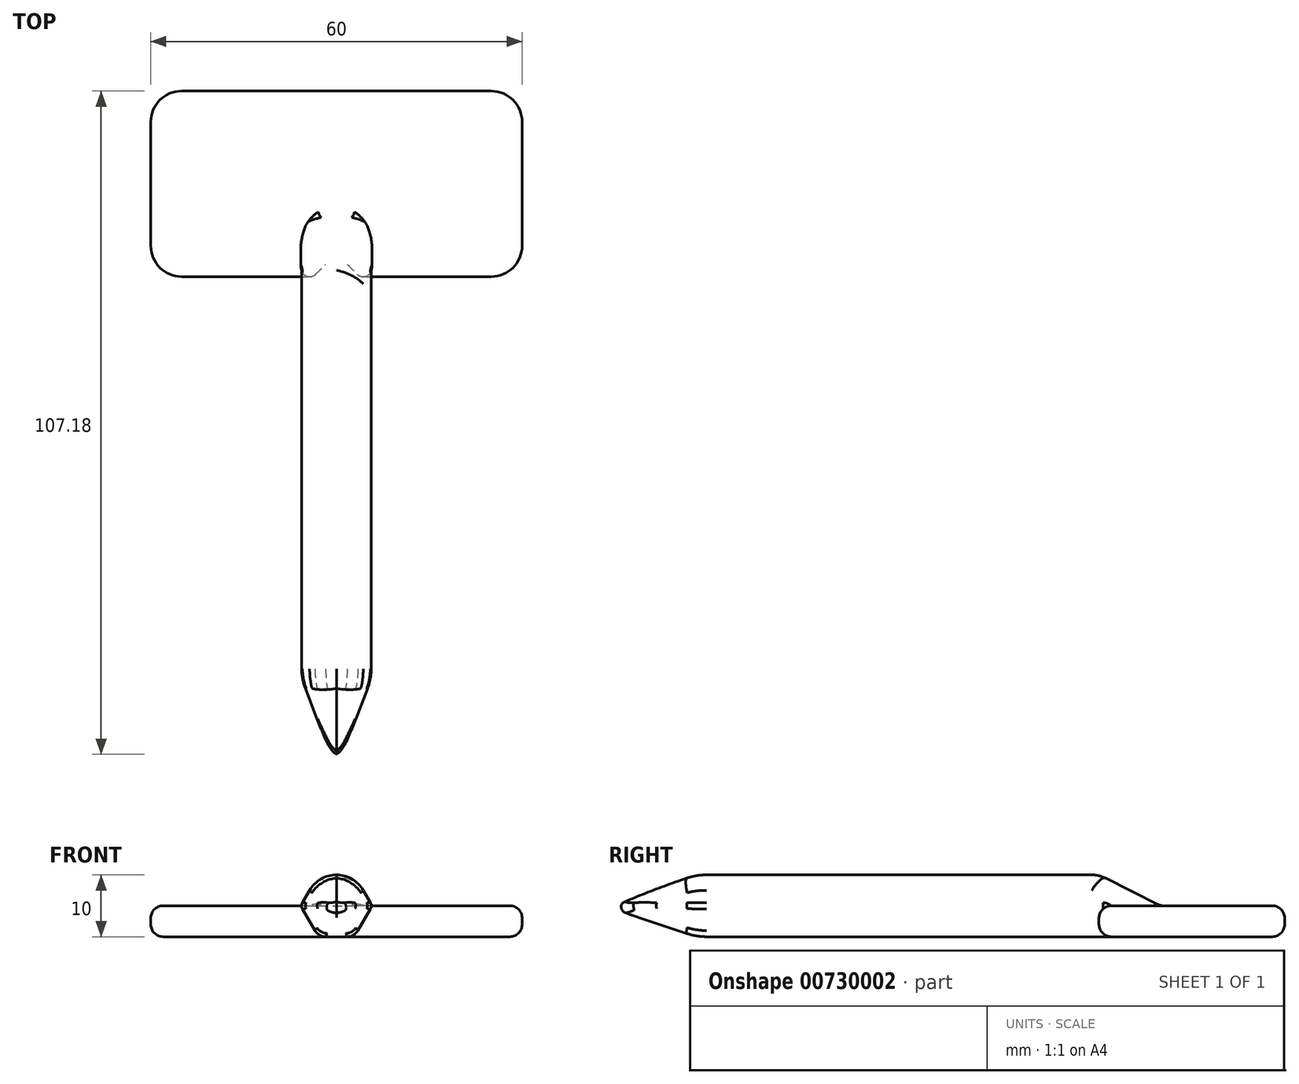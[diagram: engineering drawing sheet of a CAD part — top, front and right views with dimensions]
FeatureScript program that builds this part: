
annotation { "Feature Type Name" : "Feature", "Feature Type Description" : "" }
export const myFeature = defineFeature(function(context is Context, id is Id, definition is map)
    precondition{}
    {
        {
            var Q0;
            Q0=qCreatedBy(makeId("Top.planeOp"),FACE);
            var sketch = newSketch(context, id + "F0", { "sketchPlane" : qUnion([Q0])});
            skLineSegment(sketch, "E0.bottom", {"start": v(-30, 15) * mm, "end": v(30, 15) * mm});
            skLineSegment(sketch, "E0.top", {"start": v(-30, -15) * mm, "end": v(30, -15) * mm});
            skLineSegment(sketch, "E0.left", {"start": v(-30, 15) * mm, "end": v(-30, -15) * mm});
            skLineSegment(sketch, "E0.right", {"start": v(30, 15) * mm, "end": v(30, -15) * mm});
            skPoint(sketch, "E0.middle", {"position": v(0, 0) * mm});
            skSolve(sketch);
        }
        {
            var Q0;
            Q0=makeQuery(id+"F0.imprint","IMPRINT",FACE,{"disambiguationData":[TD([[makeQuery(id+"F0.imprint","IMPRINT",EDGE,{"derivedFrom":sQuery(id+"F0.wireOp",EDGE,"E0.bottom")}),-1.0]])]});
            extrude(context, id + "F1", {"entities" : qUnion([Q0]), "depth" : 5 * mm, "offsetDistance" : 25 * mm});
        }
        {
            var Q0;
            Q0=makeQuery(id+"F1.opExtrude","SWEPT_FACE",FACE,{"disambiguationData":[OSD([sQuery(id+"F0.wireOp",EDGE,"E0.top")])]});
            var sketch = newSketch(context, id + "F2", { "sketchPlane" : qUnion([Q0])});
            skCircle(sketch, "E1.cCircle", {"center": v(0, 5) * mm, "radius": 5 * mm, "construction": true});
            skLineSegment(sketch, "E1.0", {"start": v(5.77, 5) * mm, "end": v(2.89, 0) * mm});
            skLineSegment(sketch, "E1.1", {"start": v(2.89, 0) * mm, "end": v(-2.89, 0) * mm});
            skLineSegment(sketch, "E1.2", {"start": v(-2.89, 0) * mm, "end": v(-5.77, 5) * mm});
            skLineSegment(sketch, "E1.3", {"start": v(-5.77, 5) * mm, "end": v(-2.89, 10) * mm});
            skLineSegment(sketch, "E1.4", {"start": v(-2.89, 10) * mm, "end": v(2.89, 10) * mm});
            skLineSegment(sketch, "E1.5", {"start": v(2.89, 10) * mm, "end": v(5.77, 5) * mm});
            skPoint(sketch, "E1.0.midPoint", {"position": v(4.33, 2.5) * mm});
            skSolve(sketch);
        }
        {
            var Q0;
            {var subQ0=sQuery(id+"F2.wireOp",EDGE,"E1.3");Q0=makeQuery(id+"F2.imprint","IMPRINT",FACE,{"disambiguationData":[TD([[makeQuery(id+"F2.imprint","IMPRINT",EDGE,{"derivedFrom":subQ0}),-1.0]])]});}
            var Q1;
            {var subQ0=sQuery(id+"F2.wireOp",EDGE,"E1.0");Q1=makeQuery(id+"F2.imprint","IMPRINT",FACE,{"disambiguationData":[TD([[makeQuery(id+"F2.imprint","IMPRINT",EDGE,{"derivedFrom":subQ0}),-1.0]])]});}
            extrude(context, id + "F3", {"entities" : qUnion([Q0, Q1]), "operationType" : NewBodyOperationType.ADD, "depth" : 80 * mm, "offsetDistance" : 25 * mm, "hasSecondDirection" : true, "secondDirectionOppositeDirection" : true, "secondDirectionDepth" : 10 * mm});
        }
        {
            var Q0;
            Q0=makeQuery(id+"F1.opExtrude","SWEPT_EDGE",EDGE,{"disambiguationData":[OSD([sQuery(id+"F0.wireOp",EDGE,"E0.bottom"),sQuery(id+"F0.wireOp",EDGE,"E0.left")])]});
            var Q1;
            Q1=makeQuery(id+"F1.opExtrude","SWEPT_EDGE",EDGE,{"disambiguationData":[OSD([sQuery(id+"F0.wireOp",EDGE,"E0.bottom"),sQuery(id+"F0.wireOp",EDGE,"E0.right")])]});
            var Q2;
            Q2=makeQuery(id+"F1.opExtrude","SWEPT_EDGE",EDGE,{"disambiguationData":[OSD([sQuery(id+"F0.wireOp",EDGE,"E0.top"),sQuery(id+"F0.wireOp",EDGE,"E0.right")])]});
            var Q3;
            Q3=makeQuery(id+"F1.opExtrude","SWEPT_EDGE",EDGE,{"disambiguationData":[OSD([sQuery(id+"F0.wireOp",EDGE,"E0.top"),sQuery(id+"F0.wireOp",EDGE,"E0.left")])]});
            fillet(context, id + "F4", {"entities" : qUnion([Q0, Q1, Q2, Q3]), "radius" : 5 * mm, "tangentPropagation" : true, "allowEdgeOverflow" : false});
        }
        {
            var Q0;
            Q0=makeQuery(id+"F3.opExtrude","CAP_FACE",FACE,{"disambiguationData":[OSD([sQuery(id+"F2.wireOp",EDGE,"E1.0"),sQuery(id+"F2.wireOp",EDGE,"E1.1"),sQuery(id+"F2.wireOp",EDGE,"E1.2"),sQuery(id+"F2.wireOp",EDGE,"E1.3"),sQuery(id+"F2.wireOp",EDGE,"E1.4"),sQuery(id+"F2.wireOp",EDGE,"E1.5")])],"isStart":false});
            chamfer(context, id + "F5", {"entities" : qUnion([Q0]), "chamferType" : ChamferType.TWO_OFFSETS, "width1" : 15 * mm, "oppositeDirection" : false, "width2" : 5 * mm, "tangentPropagation" : true});
        }
        {
            var Q0;
            {var subQ0=sQuery(id+"F2.wireOp",EDGE,"E1.3");Q0=makeQuery(id+"F5.opChamfer","BLEND_EDGE",EDGE,{"blendedFrom":[makeQuery(id+"F3.opExtrude","CAP_EDGE",EDGE,{"disambiguationData":[OSD([subQ0])],"isStart":false}),makeQuery(id+"F3.opExtrude","SWEPT_FACE",FACE,{"disambiguationData":[OSD([subQ0])]})],"blendedInto":[makeQuery(id+"F3.opExtrude","SWEPT_FACE",FACE,{"disambiguationData":[OSD([subQ0])]})]});}
            var Q1;
            {var subQ0=sQuery(id+"F2.wireOp",EDGE,"E1.4");Q1=makeQuery(id+"F5.opChamfer","BLEND_EDGE",EDGE,{"blendedFrom":[makeQuery(id+"F3.opExtrude","CAP_EDGE",EDGE,{"disambiguationData":[OSD([subQ0])],"isStart":false}),makeQuery(id+"F3.opExtrude","SWEPT_FACE",FACE,{"disambiguationData":[OSD([subQ0])]})],"blendedInto":[makeQuery(id+"F3.opExtrude","SWEPT_FACE",FACE,{"disambiguationData":[OSD([subQ0])]})]});}
            var Q2;
            {var subQ0=sQuery(id+"F2.wireOp",EDGE,"E1.2");Q2=makeQuery(id+"F5.opChamfer","BLEND_EDGE",EDGE,{"blendedFrom":[makeQuery(id+"F3.opExtrude","CAP_EDGE",EDGE,{"disambiguationData":[OSD([subQ0])],"isStart":false}),makeQuery(id+"F3.opExtrude","SWEPT_FACE",FACE,{"disambiguationData":[OSD([subQ0])]})],"blendedInto":[makeQuery(id+"F3.opExtrude","SWEPT_FACE",FACE,{"disambiguationData":[OSD([subQ0])]})]});}
            var Q3;
            {var subQ0=sQuery(id+"F2.wireOp",EDGE,"E1.5");Q3=makeQuery(id+"F5.opChamfer","BLEND_EDGE",EDGE,{"blendedFrom":[makeQuery(id+"F3.opExtrude","CAP_EDGE",EDGE,{"disambiguationData":[OSD([subQ0])],"isStart":false}),makeQuery(id+"F3.opExtrude","SWEPT_FACE",FACE,{"disambiguationData":[OSD([subQ0])]})],"blendedInto":[makeQuery(id+"F3.opExtrude","SWEPT_FACE",FACE,{"disambiguationData":[OSD([subQ0])]})]});}
            var Q4;
            {var subQ0=sQuery(id+"F2.wireOp",EDGE,"E1.0");Q4=makeQuery(id+"F5.opChamfer","BLEND_EDGE",EDGE,{"blendedFrom":[makeQuery(id+"F3.opExtrude","CAP_EDGE",EDGE,{"disambiguationData":[OSD([subQ0])],"isStart":false}),makeQuery(id+"F3.opExtrude","SWEPT_FACE",FACE,{"disambiguationData":[OSD([subQ0])]})],"blendedInto":[makeQuery(id+"F3.opExtrude","SWEPT_FACE",FACE,{"disambiguationData":[OSD([subQ0])]})]});}
            var Q5;
            {var subQ0=sQuery(id+"F2.wireOp",EDGE,"E1.1");Q5=makeQuery(id+"F5.opChamfer","BLEND_EDGE",EDGE,{"blendedFrom":[makeQuery(id+"F3.opExtrude","CAP_EDGE",EDGE,{"disambiguationData":[OSD([subQ0])],"isStart":false}),makeQuery(id+"F3.boolean.opBoolean","MERGE",FACE,{"derivedFrom":[makeQuery(id+"F1.opExtrude","CAP_FACE",FACE,{"disambiguationData":[OSD([sQuery(id+"F0.wireOp",EDGE,"E0.bottom"),sQuery(id+"F0.wireOp",EDGE,"E0.top"),sQuery(id+"F0.wireOp",EDGE,"E0.left"),sQuery(id+"F0.wireOp",EDGE,"E0.right")])],"isStart":true}),makeQuery(id+"F3.opExtrude","SWEPT_FACE",FACE,{"disambiguationData":[OSD([subQ0])]})]})],"blendedInto":[makeQuery(id+"F3.boolean.opBoolean","MERGE",FACE,{"derivedFrom":[makeQuery(id+"F1.opExtrude","CAP_FACE",FACE,{"disambiguationData":[OSD([sQuery(id+"F0.wireOp",EDGE,"E0.bottom"),sQuery(id+"F0.wireOp",EDGE,"E0.top"),sQuery(id+"F0.wireOp",EDGE,"E0.left"),sQuery(id+"F0.wireOp",EDGE,"E0.right")])],"isStart":true}),makeQuery(id+"F3.opExtrude","SWEPT_FACE",FACE,{"disambiguationData":[OSD([subQ0])]})]})]});}
            fillet(context, id + "F6", {"entities" : qUnion([Q0, Q1, Q2, Q3, Q4, Q5]), "radius" : 10 * mm, "tangentPropagation" : true, "allowEdgeOverflow" : false});
        }
        {
            var Q0;
            Q0=makeQuery(id+"F3.opExtrude","CAP_EDGE",EDGE,{"disambiguationData":[OSD([sQuery(id+"F2.wireOp",EDGE,"E1.4")])],"isStart":true});
            chamfer(context, id + "F7", {"entities" : qUnion([Q0]), "chamferType" : ChamferType.TWO_OFFSETS, "width1" : 5 * mm, "oppositeDirection" : false, "width2" : 10 * mm, "tangentPropagation" : true});
        }
        {
            var Q0;
            Q0=makeQuery(id+"F1.opExtrude","CAP_EDGE",EDGE,{"disambiguationData":[OSD([sQuery(id+"F0.wireOp",EDGE,"E0.bottom")])],"isStart":false});
            var Q1;
            Q1=makeQuery(id+"F1.opExtrude","CAP_EDGE",EDGE,{"disambiguationData":[OSD([sQuery(id+"F0.wireOp",EDGE,"E0.left")])],"isStart":false});
            var Q2;
            Q2=makeQuery(id+"F1.opExtrude","CAP_EDGE",EDGE,{"disambiguationData":[OSD([sQuery(id+"F0.wireOp",EDGE,"E0.right")])],"isStart":false});
            var Q3;
            Q3=makeQuery(id+"F7.opChamfer","BLEND_EDGE",EDGE,{"blendedFrom":[makeQuery(id+"F3.opExtrude","CAP_EDGE",EDGE,{"disambiguationData":[OSD([sQuery(id+"F2.wireOp",EDGE,"E1.4")])],"isStart":true}),makeQuery(id+"F1.opExtrude","CAP_FACE",FACE,{"disambiguationData":[OSD([sQuery(id+"F0.wireOp",EDGE,"E0.bottom"),sQuery(id+"F0.wireOp",EDGE,"E0.top"),sQuery(id+"F0.wireOp",EDGE,"E0.left"),sQuery(id+"F0.wireOp",EDGE,"E0.right")])],"isStart":false})],"blendedInto":[makeQuery(id+"F1.opExtrude","CAP_FACE",FACE,{"disambiguationData":[OSD([sQuery(id+"F0.wireOp",EDGE,"E0.bottom"),sQuery(id+"F0.wireOp",EDGE,"E0.top"),sQuery(id+"F0.wireOp",EDGE,"E0.left"),sQuery(id+"F0.wireOp",EDGE,"E0.right")])],"isStart":false})]});
            var Q4;
            {var subQ0=sQuery(id+"F0.wireOp",EDGE,"E0.right");var subQ1=sQuery(id+"F0.wireOp",EDGE,"E0.top");Q4=makeQuery(id+"F3.boolean.opBoolean","SPLIT",EDGE,{"disambiguationData":[TD([makeQuery(id+"F1.opExtrude","SWEPT_FACE",FACE,{"disambiguationData":[OSD([subQ0])]})])],"derivedFrom":makeQuery(id+"F1.opExtrude","CAP_EDGE",EDGE,{"disambiguationData":[OSD([subQ1])],"isStart":false})});}
            var Q5;
            {var subQ0=sQuery(id+"F0.wireOp",EDGE,"E0.left");var subQ1=sQuery(id+"F0.wireOp",EDGE,"E0.top");Q5=makeQuery(id+"F3.boolean.opBoolean","SPLIT",EDGE,{"disambiguationData":[TD([makeQuery(id+"F1.opExtrude","SWEPT_FACE",FACE,{"disambiguationData":[OSD([subQ0])]})])],"derivedFrom":makeQuery(id+"F1.opExtrude","CAP_EDGE",EDGE,{"disambiguationData":[OSD([subQ1])],"isStart":false})});}
            fillet(context, id + "F8", {"entities" : qUnion([Q0, Q1, Q2, Q3, Q4, Q5]), "radius" : 2 * mm, "tangentPropagation" : true, "allowEdgeOverflow" : false});
        }
        {
            var Q0;
            Q0=makeQuery(id+"F3.boolean.opBoolean","MERGE",FACE,{"derivedFrom":[makeQuery(id+"F1.opExtrude","CAP_FACE",FACE,{"disambiguationData":[OSD([sQuery(id+"F0.wireOp",EDGE,"E0.bottom"),sQuery(id+"F0.wireOp",EDGE,"E0.top"),sQuery(id+"F0.wireOp",EDGE,"E0.left"),sQuery(id+"F0.wireOp",EDGE,"E0.right")])],"isStart":true}),makeQuery(id+"F3.opExtrude","SWEPT_FACE",FACE,{"disambiguationData":[OSD([sQuery(id+"F2.wireOp",EDGE,"E1.1")])]})]});
            fillet(context, id + "F9", {"entities" : qUnion([Q0]), "radius" : 2 * mm, "tangentPropagation" : true, "allowEdgeOverflow" : false});
        }
        {
            var Q0;
            Q0=makeQuery(id+"F7.opChamfer","BLEND_EDGE",EDGE,{"blendedFrom":[makeQuery(id+"F3.opExtrude","CAP_EDGE",EDGE,{"disambiguationData":[OSD([sQuery(id+"F2.wireOp",EDGE,"E1.4")])],"isStart":true}),makeQuery(id+"F3.opExtrude","SWEPT_FACE",FACE,{"disambiguationData":[OSD([sQuery(id+"F2.wireOp",EDGE,"E1.5")])]})],"blendedInto":[makeQuery(id+"F3.opExtrude","SWEPT_FACE",FACE,{"disambiguationData":[OSD([sQuery(id+"F2.wireOp",EDGE,"E1.5")])]})]});
            var Q1;
            Q1=makeQuery(id+"F7.opChamfer","BLEND_EDGE",EDGE,{"blendedFrom":[makeQuery(id+"F3.opExtrude","CAP_EDGE",EDGE,{"disambiguationData":[OSD([sQuery(id+"F2.wireOp",EDGE,"E1.4")])],"isStart":true}),makeQuery(id+"F3.opExtrude","SWEPT_FACE",FACE,{"disambiguationData":[OSD([sQuery(id+"F2.wireOp",EDGE,"E1.3")])]})],"blendedInto":[makeQuery(id+"F3.opExtrude","SWEPT_FACE",FACE,{"disambiguationData":[OSD([sQuery(id+"F2.wireOp",EDGE,"E1.3")])]})]});
            var Q2;
            Q2=makeQuery(id+"F3.opExtrude","SWEPT_FACE",FACE,{"disambiguationData":[OSD([sQuery(id+"F2.wireOp",EDGE,"E1.4")])]});
            fillet(context, id + "F10", {"entities" : qUnion([Q0, Q1, Q2]), "radius" : 5 * mm, "tangentPropagation" : true, "allowEdgeOverflow" : false});
        }
        {
            var Q0;
            {var subQ0=sQuery(id+"F2.wireOp",EDGE,"E1.2");var subQ1=sQuery(id+"F2.wireOp",EDGE,"E1.3");Q0=makeQuery(id+"F3.boolean.opBoolean","SPLIT",EDGE,{"disambiguationData":[topologyDisambiguationEdgeConnected([makeQuery(id+"F3.opExtrude","SWEPT_FACE",FACE,{"disambiguationData":[OSD([subQ0])]})])],"derivedFrom":makeQuery(id+"F3.opExtrude","SWEPT_EDGE",EDGE,{"disambiguationData":[OSD([sQuery(id+"F0.wireOp",EDGE,"E0.top"),subQ0,subQ1])]})});}
            var Q1;
            {var subQ0=sQuery(id+"F2.wireOp",EDGE,"E1.0");var subQ1=sQuery(id+"F2.wireOp",EDGE,"E1.5");Q1=makeQuery(id+"F3.boolean.opBoolean","SPLIT",EDGE,{"disambiguationData":[topologyDisambiguationEdgeConnected([makeQuery(id+"F3.opExtrude","SWEPT_FACE",FACE,{"disambiguationData":[OSD([subQ0])]})])],"derivedFrom":makeQuery(id+"F3.opExtrude","SWEPT_EDGE",EDGE,{"disambiguationData":[OSD([sQuery(id+"F0.wireOp",EDGE,"E0.top"),subQ0,subQ1])]})});}
            fillet(context, id + "F11", {"entities" : qUnion([Q0, Q1]), "radius" : 1 * mm, "tangentPropagation" : true, "allowEdgeOverflow" : false});
        }
    });
